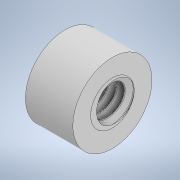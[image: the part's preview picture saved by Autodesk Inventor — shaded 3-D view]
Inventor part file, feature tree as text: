
AUTODESK INVENTOR PART (.ipt)
format: ipt  version: 2020 (Build 240168000, 168)  size: 413,696 bytes
history: native  units: mm
features: sketch x4, extrude x2, revolve x1, helix x1
ambient origin geometry x8: Origin, YZ Plane, XZ Plane, XY Plane, X Axis, Y Axis, Z Axis, Center Point
bodies: Solid1 (feature_tree), Solid7 (feature_tree)
feature tree (8):
  extrude  "Extrusion1"  Depth=6.0mm TaperAngle=0.0deg
  extrude  "Extrusion2"  Depth=3.0mm TaperAngle=0.0deg
  revolve  "Revolution6"  [1 undecoded]
  helix  "Coil6"  [1 undecoded]
  sketch  "Sketch1"  dims[d0=10.0mm d1=6.0mm d2=0.0mm]
  sketch  "Sketch2"  dims[d3=5.5mm d4=3.0mm d5=0.0mm]
  sketch  "Sketch14"  dims[d17=9.599311mm d37=9.599311mm d57=9.599311mm]
  sketch  "Sketch15"  dims[d77=9.599311mm d97=9.599311mm d110=9.599311mm d111=0.160083mm d112=0.160083mm d115=1.0mm d117=9.599311mm d119=0.0mm d120=1.001mm d121=5.0mm d122=10.0mm d123=0.0mm d124=0.0mm d125=0.0mm d126=0.0mm d127=0.0mm]
note: 2 required parameter values undecoded (feature->parameter linkage not recoverable at this tier; creation-order binding heuristic only, values carry confidence <= 0.55)